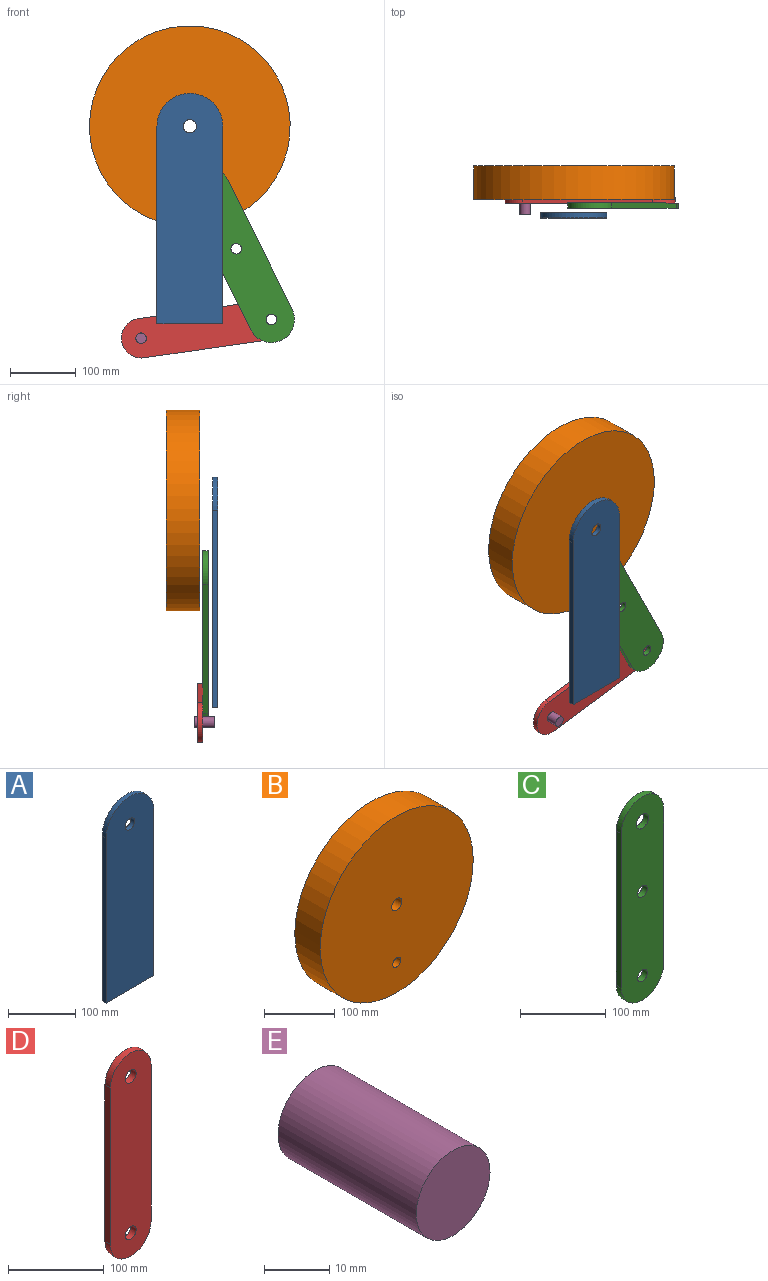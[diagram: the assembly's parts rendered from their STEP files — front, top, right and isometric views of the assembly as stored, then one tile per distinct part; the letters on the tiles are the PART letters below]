
ASSEMBLY  parts=5 mates=4
PART A: 7 faces, bbox 100x8x350 mm
  f0: plane 300x8mm, normal (1,0,0), area 2400mm2, adj f1,f3,f5,f6
  f1: cylinder r=50mm len=100mm, axis (0,1,0), area 1256.6mm2, adj f0,f2,f5,f6
  f2: plane 300x8mm, normal (-1,0,0), area 2400mm2, adj f1,f3,f5,f6
  f3: plane 100x8mm, normal (0,0,-1), area 800mm2, adj f0,f2,f5,f6
  f4: cylinder r=10mm len=20mm, axis (0,1,0), area 502.7mm2, adj f5,f6
  f5: plane 350x100mm, normal (0,-1,0), area 33612.8mm2, adj f0,f1,f2,f3,f4
  f6: plane 350x100mm, normal (0,1,0), area 33612.8mm2, adj f0,f1,f2,f3,f4
PART B: 5 faces, bbox 304.8x50.8x304.8 mm
  f0: cylinder r=152.4mm len=304.8mm, axis (0,-1,0), area 48643.9mm2, adj f1,f2
  f1: plane 304.8x304.8mm, normal (0,1,0), area 72450.7mm2, adj f0,f3,f4
  f2: plane 304.8x304.8mm, normal (0,-1,0), area 72450.7mm2, adj f0,f3,f4
  f3: cylinder r=8mm len=50.8mm, axis (0,-1,0), area 2553.5mm2, adj f1,f2
  f4: cylinder r=10mm len=50.8mm, axis (0,-1,0), area 3191.9mm2, adj f1,f2
PART C: 9 faces, bbox 70x8x290 mm
  f0: plane 220x8mm, normal (1,0,0), area 1760mm2, adj f1,f5,f6,f7
  f1: cylinder r=35mm len=70mm, axis (0,1,0), area 879.6mm2, adj f0,f2,f6,f7
  f2: plane 220x8mm, normal (-1,0,0), area 1760mm2, adj f1,f5,f6,f7
  f3: cylinder r=8mm len=16mm, axis (0,1,0), area 402.1mm2, adj f6,f7
  f4: cylinder r=8mm len=16mm, axis (0,1,0), area 402.1mm2, adj f6,f7
  f5: cylinder r=35mm len=70mm, axis (0,1,0), area 879.6mm2, adj f0,f2,f6,f7
  f6: plane 290x70mm, normal (0,-1,0), area 18532.2mm2, adj f0,f1,f2,f3,f4,f5,f8
  f7: plane 290x70mm, normal (0,1,0), area 18532.2mm2, adj f0,f1,f2,f3,f4,f5,f8
  f8: cylinder r=10mm len=20mm, axis (0,-1,0), area 502.7mm2, adj f6,f7
PART D: 8 faces, bbox 60x8x260 mm
  f0: cylinder r=30mm len=60mm, axis (0,-1,0), area 754mm2, adj f1,f4,f6,f7
  f1: plane 200x8mm, normal (-1,0,0), area 1600mm2, adj f0,f2,f6,f7
  f2: cylinder r=30mm len=60mm, axis (0,-1,0), area 754mm2, adj f1,f4,f6,f7
  f3: cylinder r=8mm len=16mm, axis (0,-1,0), area 402.1mm2, adj f6,f7
  f4: plane 200x8mm, normal (1,0,0), area 1600mm2, adj f0,f2,f6,f7
  f5: cylinder r=8mm len=16mm, axis (0,-1,0), area 402.1mm2, adj f6,f7
  f6: plane 260x60mm, normal (0,1,0), area 14425.3mm2, adj f0,f1,f2,f3,f4,f5
  f7: plane 260x60mm, normal (0,-1,0), area 14425.3mm2, adj f0,f1,f2,f3,f4,f5
PART E: 3 faces, bbox 16x30x16 mm
  f0: cylinder r=8mm len=30mm, axis (0,1,0), area 1508mm2, adj f1,f2
  f1: plane 16x16mm, normal (0,-1,0), area 201.1mm2, adj f0
  f2: plane 16x16mm, normal (0,1,0), area 201.1mm2, adj f0
PLACE A at identity fixed
PLACE B rot(axis=(0,-1,0),15deg) t=(0,2,0)mm
PLACE C rot(axis=(0,-1,0),26.5deg) t=(25.9,2,-96.59)mm
PLACE D rot(axis=(0,1,0),81.8deg) t=(341.71,2,-262.18)mm
PLACE E rot(axis=(0,1,0),96.3deg) t=(343.45,-0.81,-368.18)mm fixed
MATE revolute A.f4 <-> B.f0  axis (0,1,0) through (0,-18,0)mm
MATE revolute C.f8 <-> B.f3  axis (0,-1,0) through (25.9,-3,-96.59)mm
MATE revolute D.f5 <-> C.f5  axis (0,-1,0) through (123.95,-3,-293.53)mm
MATE cylindrical E.f0 <-> D.f0  axis (0,1,0) through (-74.01,9.19,-322.02)mm
